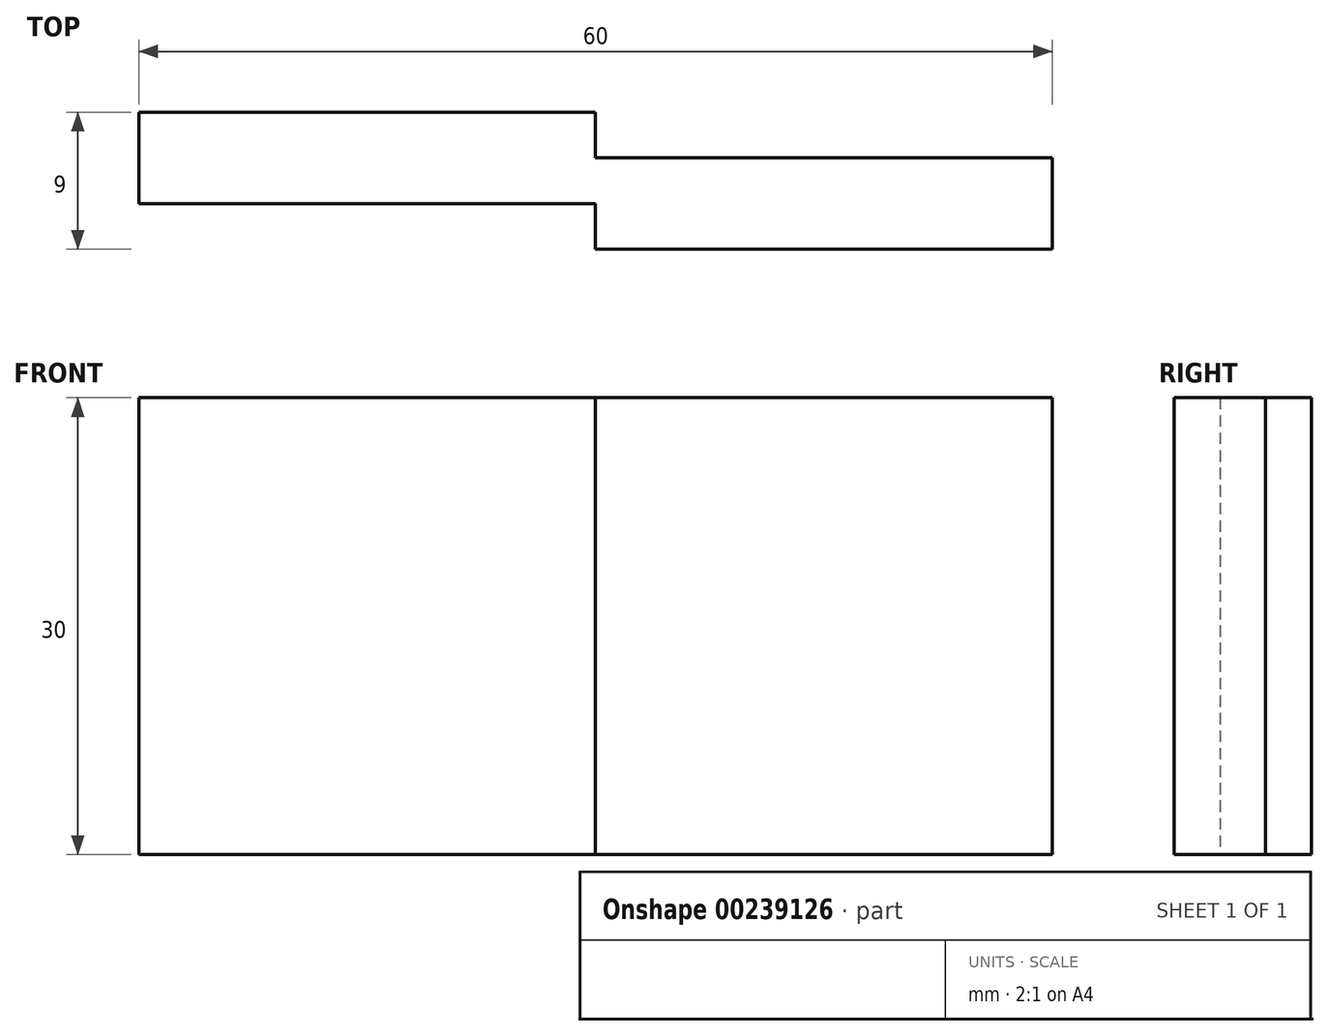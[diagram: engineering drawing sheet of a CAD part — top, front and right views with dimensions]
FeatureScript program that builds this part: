
annotation { "Feature Type Name" : "Feature", "Feature Type Description" : "" }
export const myFeature = defineFeature(function(context is Context, id is Id, definition is map)
    precondition{}
    {
        {
            assignVariable(context, id + "F0", {"name" : "v", "anyValue" : 3});
        }
        {
            var Q0;
            Q0=qCreatedBy(makeId("Front.planeOp"),FACE);
            var sketch = newSketch(context, id + "F1", { "sketchPlane" : qUnion([Q0])});
            skLineSegment(sketch, "E0.bottom", {"start": v(15, 15) * mm, "end": v(-15, 15) * mm});
            skLineSegment(sketch, "E0.top", {"start": v(15, -15) * mm, "end": v(-15, -15) * mm});
            skLineSegment(sketch, "E0.left", {"start": v(15, 15) * mm, "end": v(15, -15) * mm});
            skLineSegment(sketch, "E0.right", {"start": v(-15, 15) * mm, "end": v(-15, -15) * mm});
            skPoint(sketch, "E0.middle", {"position": v(0, 0) * mm});
            skSolve(sketch);
        }
        {
            var Q0;
            Q0=qSketchRegion(id+"F1",true);
            extrude(context, id + "F2", {"entities" : qUnion([Q0]), "endBound" : BoundingType.SYMMETRIC, "depth" : (2 * getVariable(context, 'v')) * mm});
        }
        {
            var Q0;
            Q0=makeQuery(id+"F2.opExtrude","CAP_FACE",FACE,{"disambiguationData":[OSD([sQuery(id+"F1.wireOp",EDGE,"E0.bottom"),sQuery(id+"F1.wireOp",EDGE,"E0.top"),sQuery(id+"F1.wireOp",EDGE,"E0.left"),sQuery(id+"F1.wireOp",EDGE,"E0.right")])],"isStart":false});
            var sketch = newSketch(context, id + "F3", { "sketchPlane" : qUnion([Q0])});
            skLineSegment(sketch, "E1.bottom", {"start": v(15, 15) * mm, "end": v(45, 15) * mm});
            skLineSegment(sketch, "E1.top", {"start": v(15, -15) * mm, "end": v(45, -15) * mm});
            skLineSegment(sketch, "E1.left", {"start": v(15, 15) * mm, "end": v(15, -15) * mm});
            skLineSegment(sketch, "E1.right", {"start": v(45, 15) * mm, "end": v(45, -15) * mm});
            skSolve(sketch);
        }
        {
            var Q0;
            Q0=qSketchRegion(id+"F3",true);
            extrude(context, id + "F4", {"entities" : qUnion([Q0]), "operationType" : NewBodyOperationType.ADD, "endBound" : BoundingType.SYMMETRIC, "oppositeDirection" : true, "depth" : (2 * getVariable(context, 'v')) * mm});
        }
    });
